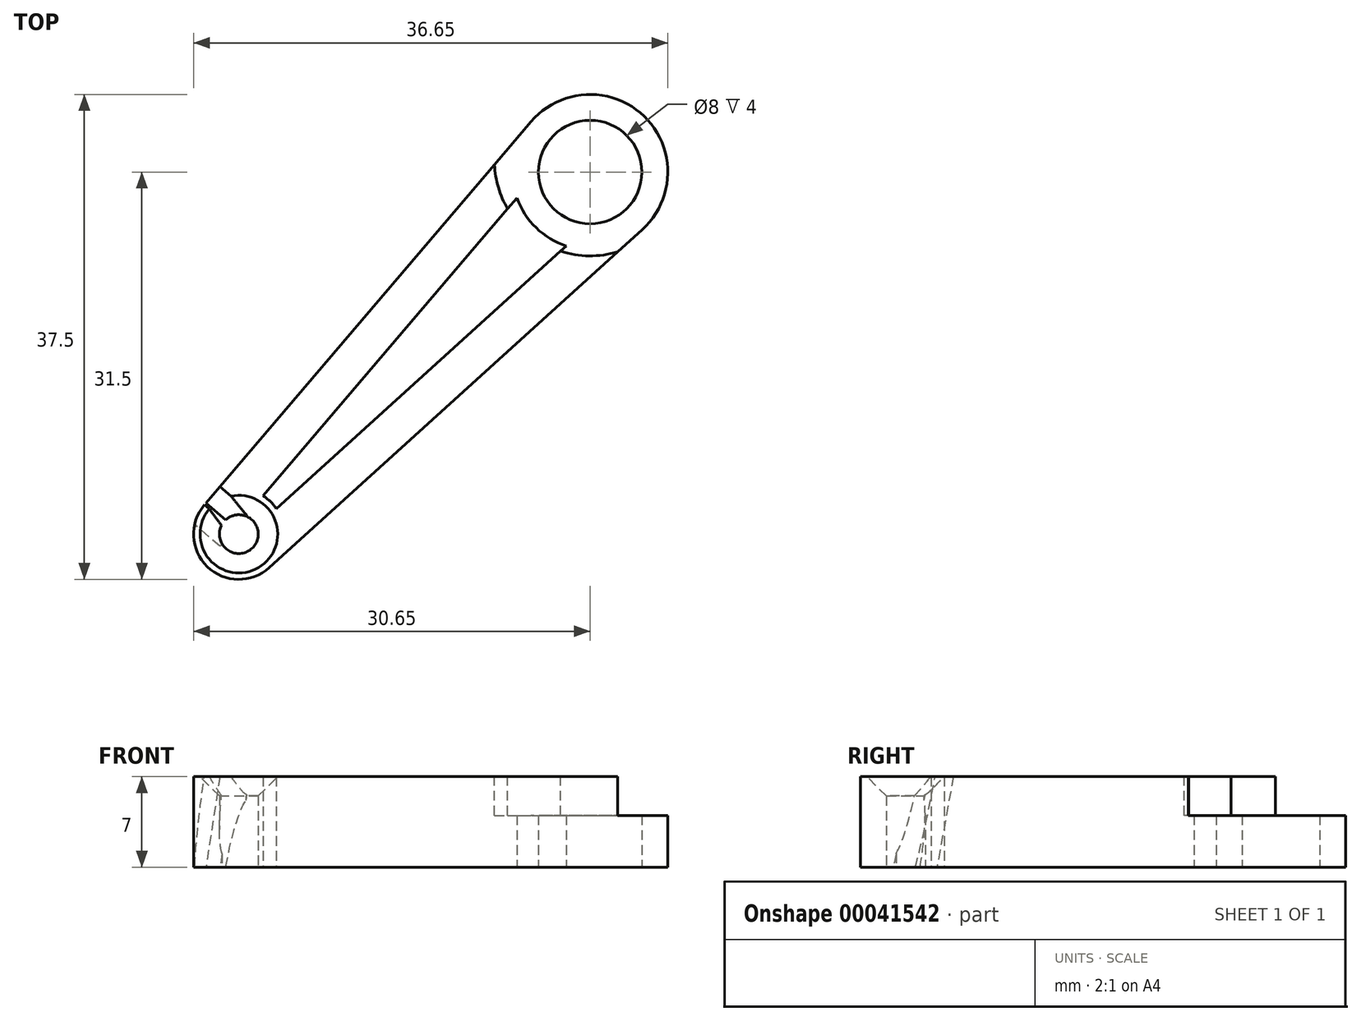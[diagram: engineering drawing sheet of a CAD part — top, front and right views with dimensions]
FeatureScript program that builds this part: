
annotation { "Feature Type Name" : "Feature", "Feature Type Description" : "" }
export const myFeature = defineFeature(function(context is Context, id is Id, definition is map)
    precondition{}
    {
        {
            var Q0;
            Q0=qCreatedBy(makeId("Top.planeOp"),FACE);
            var sketch = newSketch(context, id + "F0", { "sketchPlane" : qUnion([Q0])});
            skCircle(sketch, "E0", {"center": v(0, 0) * mm, "radius": 4 * mm});
            skCircle(sketch, "E1", {"center": v(0, 0) * mm, "radius": 6 * mm});
            skLineSegment(sketch, "E2", {"start": v(0, 0) * mm, "end": v(-27.15, 0) * mm, "construction": true});
            skLineSegment(sketch, "E3", {"start": v(-27.15, 0) * mm, "end": v(-27.15, -28) * mm, "construction": true});
            skCircle(sketch, "E4", {"center": v(-27.15, -28) * mm, "radius": 3.5 * mm});
            skCircle(sketch, "E5", {"center": v(-27.15, -28) * mm, "radius": 1.5 * mm});
            skLineSegment(sketch, "E6", {"start": v(-29.81, -25.73) * mm, "end": v(-4.57, 3.9) * mm});
            skLineSegment(sketch, "E7", {"start": v(-24.8, -30.6) * mm, "end": v(4.03, -4.44) * mm});
            skLineSegment(sketch, "E8", {"start": v(0, 0) * mm, "end": v(-27.15, -28) * mm, "construction": true});
            skLineSegment(sketch, "E9.trimOffspring", {"start": v(-25.28, -25.04) * mm, "end": v(-5.65, -2) * mm});
            skLineSegment(sketch, "E10.trimOffspring", {"start": v(-24.25, -26.04) * mm, "end": v(-1.83, -5.71) * mm});
            skSolve(sketch);
        }
        {
            var Q0;
            Q0 = qSketchRegion(id + "F0", true);
            extrude(context, id + "F1", {"entities" : qUnion([Q0]), "depth" : 7 * mm});
        }
        {
            var Q0;
            Q0=makeQuery(id+"F1.opExtrude","CAP_FACE",FACE,{"disambiguationData":[OSD([sQuery(id+"F0.wireOp",EDGE,"E0"),sQuery(id+"F0.wireOp",EDGE,"E1"),sQuery(id+"F0.wireOp",EDGE,"E4"),sQuery(id+"F0.wireOp",EDGE,"E5"),sQuery(id+"F0.wireOp",EDGE,"E6"),sQuery(id+"F0.wireOp",EDGE,"E7"),sQuery(id+"F0.wireOp",EDGE,"955353e0-da7d-4a69-9bc8-f35965b1859a.trimOffspring"),sQuery(id+"F0.wireOp",EDGE,"f0f998e1-acde-457c-a012-71004b5fe20b.trimOffspring")])],"isStart":false});
            var sketch = newSketch(context, id + "F2", { "sketchPlane" : qUnion([Q0])});
            skCircle(sketch, "E11", {"center": v(0, 0.92) * mm, "radius": 7.4 * mm});
            skSolve(sketch);
        }
        {
            var Q0;
            Q0 = qSketchRegion(id + "F2", true);
            extrude(context, id + "F3", {"entities" : qUnion([Q0]), "operationType" : NewBodyOperationType.REMOVE, "oppositeDirection" : true, "depth" : 3 * mm});
        }
        {
            var Q0;
            Q0=makeQuery(id+"F1.opExtrude","CAP_EDGE",EDGE,{"disambiguationData":[OSD([sQuery(id+"F0.wireOp",EDGE,"E5")])],"isStart":false});
            chamfer(context, id + "F4", {"entities" : qUnion([Q0]), "width" : 1.5 * mm, "tangentPropagation" : true});
        }
        {
            var Q0;
            Q0=makeQuery(id+"F1.opExtrude","SWEPT_FACE",FACE,{"disambiguationData":[OSD([sQuery(id+"F0.wireOp",EDGE,"E6")])]});
            var sketch = newSketch(context, id + "F5", { "sketchPlane" : qUnion([Q0])});
            skLineSegment(sketch, "E12", {"start": v(38.92, 7) * mm, "end": v(40.58, 0) * mm});
            skLineSegment(sketch, "E13.0", {"start": v(37.07, 7) * mm, "end": v(38.73, 0) * mm});
            skLineSegment(sketch, "E14", {"start": v(38.92, 0) * mm, "end": v(40.58, 0) * mm});
            skLineSegment(sketch, "E15", {"start": v(38.92, 7) * mm, "end": v(37.07, 7) * mm});
            skSolve(sketch);
        }
        {
            var Q0;
            Q0=makeQuery(id+"F5.imprint","IMPRINT",FACE,{"disambiguationData":[TD([[makeQuery(id+"F5.imprint","IMPRINT",EDGE,{"derivedFrom":sQuery(id+"F5.wireOp",EDGE,"E12")}),-1.0]])]});
            var Q1;
            {var subQ0=sQuery(id+"F0.wireOp",EDGE,"E6");var subQ4=makeQuery(id+"F1.opExtrude","SWEPT_EDGE",EDGE,{"disambiguationData":[OSD([sQuery(id+"F0.wireOp",EDGE,"E4"),subQ0])]});Q1=makeQuery(id+"F5.imprint","IMPRINT",FACE,{"disambiguationData":[TD([[makeQuery(id+"F5.imprint","IMPRINT",EDGE,{"derivedFrom":subQ4}),-1.0]])]});}
            var Q2;
            Q2=makeQuery(id+"F1.opExtrude","SWEPT_FACE",FACE,{"disambiguationData":[OSD([sQuery(id+"F0.wireOp",EDGE,"E5")])]});
            extrude(context, id + "F6", {"entities" : qUnion([Q0, Q1]), "operationType" : NewBodyOperationType.REMOVE, "oppositeDirection" : true, "endBoundEntityFace" : qUnion([Q2]), "depth" : 3 * mm});
        }
    });
